# Revit family: Accessory-Towel_Bar-KOHLER-STRAYT-K-37347T_1
name_source: partatom
category: Specialty Equipment
revit_build: Autodesk Revit 2017 (Build: 20160225_1515(x64)
units: mm (PartAtom-declared; Revit-internal decimal feet)

## family parameters
Cut with Voids When Loaded = No
Host = Face
OmniClass Number = 23.40.20.21.27
OmniClass Title = Towel Bars
Part Type = Normal
Room Calculation Point = No
Round Connector Dimension = Use Diameter
Shared = No

## types (3) — shared parameters
ADA Compliant = No
Assembly Code = C1030200
Date Modified = 08/28/2020
Default Elevation = 42"
Description = STRAYT Slei 24
Finish = Kohler-Metal-CP-Polished_Chrome
Height = 15/16"
Length = 2 13/16"
Manufacturer = KOHLER Co.
Master Format 2014 = 10 28 00
Master Format 2014 Name = Toilet, Bath, and Laundry Accessories
Material = Solid Brass Construction
Product Documentation Link = https://files.kohler.com.cn
Product Name = STRAYT
Product Page URL = https://www.kohler.com.cn
URL = http://www.kohler.com.cn
WaterSense Certified = No
Width = 24"

## per-type parameters (varying)
| type | Model | Patern Design | Red Color | Type | White Color | Without Patern |
| CP-Polished Chrome | K-37347T-CP | No | No | 1 | No | Yes |
| DPR, CP-Polished Chrome | K-37347T-DPR-CP | Yes | Yes | 2 | No | No |
| DPW, CP-Polished Chrome | K-37347T-DPW-CP | Yes | No | 3 | Yes | No |

## geometry (parser evidence)
native form markers: Sweep x6
no freeform markers — native parametric forms only
